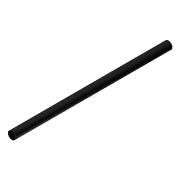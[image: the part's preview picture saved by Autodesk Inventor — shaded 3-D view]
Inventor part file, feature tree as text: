
AUTODESK INVENTOR PART (.ipt)
format: ipt  version: unknown  size: 155,136 bytes
history: native  units: in
note: dims shown in document units (in); Inventor stores cm internally (conversion verified against a paired STEP export)
features: extrude x1, sketch x1
ambient origin geometry x8: Origin, YZ Plane, XZ Plane, XY Plane, X Axis, Y Axis, Z Axis, Center Point
feature tree (2):
  extrude  "Extrusion5"  Depth=0.7874in TaperAngle=0.0deg
  sketch  "Sketch15"  dims[d33=0.0394in d34=0.7874in d35=0.0in]
